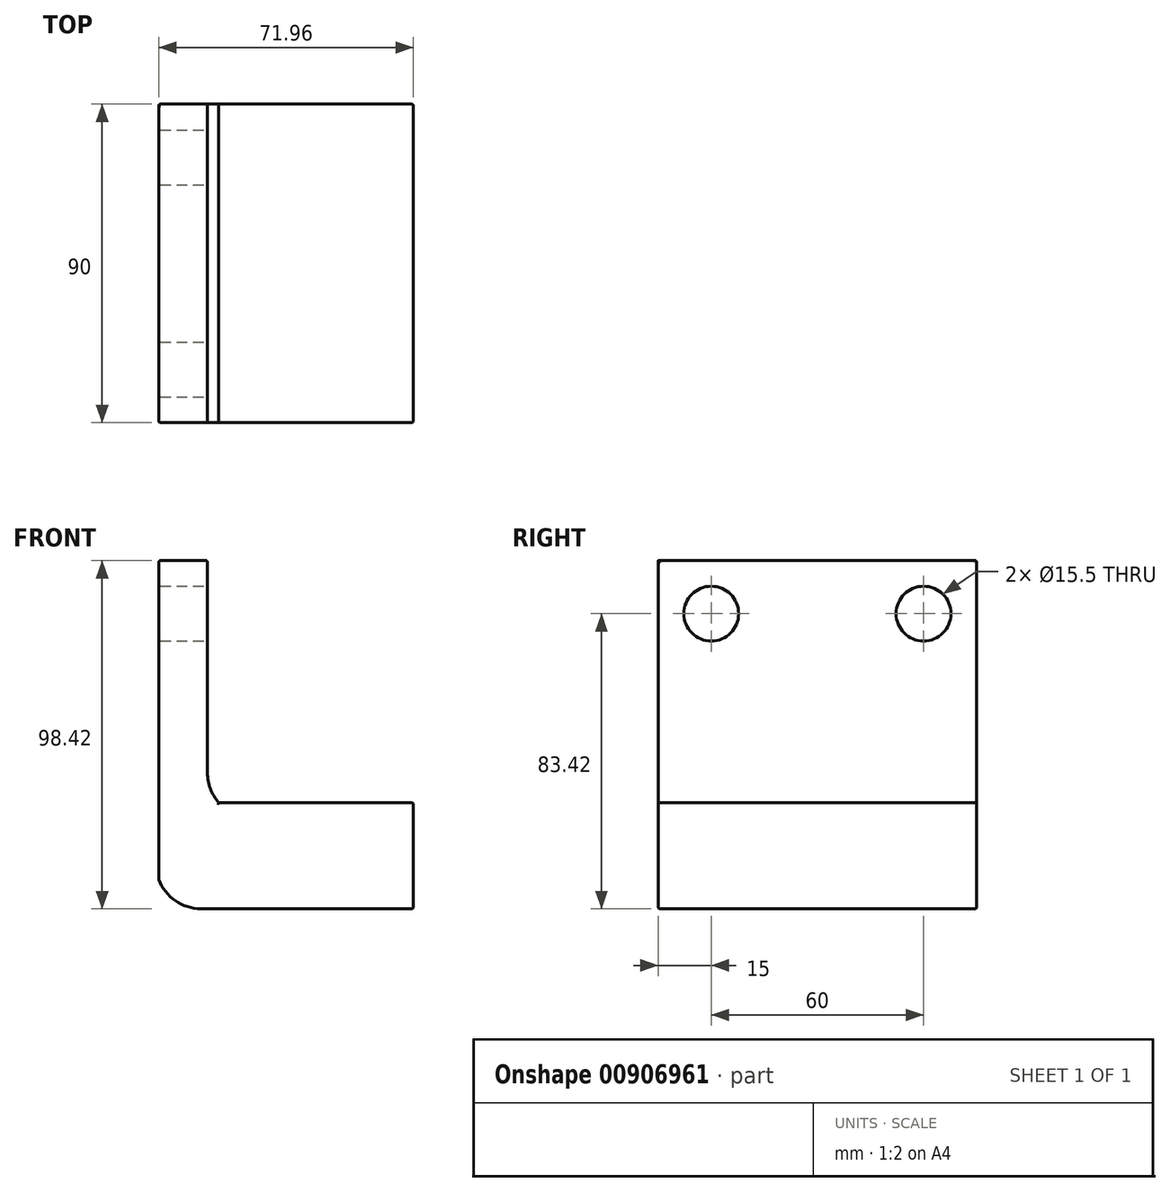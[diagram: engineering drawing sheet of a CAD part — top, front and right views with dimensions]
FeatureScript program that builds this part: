
annotation { "Feature Type Name" : "Feature", "Feature Type Description" : "" }
export const myFeature = defineFeature(function(context is Context, id is Id, definition is map)
    precondition{}
    {
        {
            var Q0;
            Q0=qCreatedBy(makeId("Front.planeOp"),FACE);
            var sketch = newSketch(context, id + "F0", { "sketchPlane" : qUnion([Q0])});
            skLineSegment(sketch, "E0", {"start": v(-41.34, 51.99) * mm, "end": v(-41.34, -21.08) * mm});
            skLineSegment(sketch, "E1", {"start": v(-41.34, 51.99) * mm, "end": v(-27.58, 51.99) * mm});
            skLineSegment(sketch, "E2", {"start": v(-27.58, 51.99) * mm, "end": v(-27.58, -8.01) * mm});
            skLineSegment(sketch, "E3", {"start": v(-24.38, -16.43) * mm, "end": v(30.62, -16.43) * mm});
            skLineSegment(sketch, "E4", {"start": v(30.62, -16.43) * mm, "end": v(30.62, -46.43) * mm});
            skLineSegment(sketch, "E5", {"start": v(30.62, -46.43) * mm, "end": v(-29.38, -46.43) * mm});
            skLineSegment(sketch, "E6", {"start": v(-41.34, -21.08) * mm, "end": v(-41.34, -38.01) * mm});
            skArc(sketch, "E7", {"start": v(-27.58, -8.01) * mm, "mid": v(-26.75, -12.51) * mm, "end": v(-24.38, -16.43) * mm});
            skArc(sketch, "E8", {"start": v(-41.34, -38.01) * mm, "mid": v(-36.7, -44.12) * mm, "end": v(-29.38, -46.43) * mm});
            skSolve(sketch);
        }
        {
            var Q0;
            Q0 = qSketchRegion(id + "F0", true);
            extrude(context, id + "F1", {"entities" : qUnion([Q0]), "depth" : 90 * mm, "offsetDistance" : 25 * mm});
        }
        {
            var Q0;
            Q0=makeQuery(id+"F1.opExtrude","SWEPT_FACE",FACE,{"disambiguationData":[OSD([sQuery(id+"F0.wireOp",EDGE,"E2")])]});
            var sketch = newSketch(context, id + "F2", { "sketchPlane" : qUnion([Q0])});
            skCircle(sketch, "E9", {"center": v(-75, 36.99) * mm, "radius": 7.75 * mm});
            skCircle(sketch, "E10", {"center": v(-15, 36.99) * mm, "radius": 7.75 * mm});
            skSolve(sketch);
        }
        {
            var Q0;
            Q0 = qSketchRegion(id + "F2", true);
            extrude(context, id + "F3", {"entities" : qUnion([Q0]), "operationType" : NewBodyOperationType.REMOVE, "oppositeDirection" : true, "depth" : 25 * mm, "offsetDistance" : 25 * mm});
        }
        {
            var Q0;
            Q0=makeQuery(id+"F1.opExtrude","SWEPT_EDGE",EDGE,{"disambiguationData":[OSD([sQuery(id+"F0.wireOp",EDGE,"E1"),sQuery(id+"F0.wireOp",EDGE,"E2")])]});
            var Q1;
            Q1=makeQuery(id+"F1.opExtrude","CAP_EDGE",EDGE,{"disambiguationData":[OSD([sQuery(id+"F0.wireOp",EDGE,"E2")])],"isStart":true});
            var Q2;
            Q2=makeQuery(id+"F1.opExtrude","CAP_EDGE",EDGE,{"disambiguationData":[OSD([sQuery(id+"F0.wireOp",EDGE,"E2")])],"isStart":false});
            var Q3;
            Q3=makeQuery(id+"F1.opExtrude","SWEPT_EDGE",EDGE,{"disambiguationData":[OSD([sQuery(id+"F0.wireOp",EDGE,"E3"),sQuery(id+"F0.wireOp",EDGE,"E4")])]});
            var Q4;
            Q4=makeQuery(id+"F1.opExtrude","CAP_EDGE",EDGE,{"disambiguationData":[OSD([sQuery(id+"F0.wireOp",EDGE,"E4")])],"isStart":false});
            var Q5;
            Q5=makeQuery(id+"F1.opExtrude","SWEPT_EDGE",EDGE,{"disambiguationData":[OSD([sQuery(id+"F0.wireOp",EDGE,"E4"),sQuery(id+"F0.wireOp",EDGE,"E5")])]});
            var Q6;
            Q6=makeQuery(id+"F1.opExtrude","CAP_EDGE",EDGE,{"disambiguationData":[OSD([sQuery(id+"F0.wireOp",EDGE,"E4")])],"isStart":true});
            var Q7;
            Q7=makeQuery(id+"F1.opExtrude","CAP_EDGE",EDGE,{"disambiguationData":[OSD([sQuery(id+"F0.wireOp",EDGE,"E3")])],"isStart":true});
            var Q8;
            Q8=makeQuery(id+"F1.opExtrude","CAP_EDGE",EDGE,{"disambiguationData":[OSD([sQuery(id+"F0.wireOp",EDGE,"E5")])],"isStart":true});
            var Q9;
            Q9=makeQuery(id+"F1.opExtrude","CAP_EDGE",EDGE,{"disambiguationData":[OSD([sQuery(id+"F0.wireOp",EDGE,"E0"),sQuery(id+"F0.wireOp",EDGE,"E6")])],"isStart":true});
            var Q10;
            Q10=makeQuery(id+"F1.opExtrude","CAP_EDGE",EDGE,{"disambiguationData":[OSD([sQuery(id+"F0.wireOp",EDGE,"E1")])],"isStart":true});
            var Q11;
            Q11=makeQuery(id+"F1.opExtrude","SWEPT_EDGE",EDGE,{"disambiguationData":[OSD([sQuery(id+"F0.wireOp",EDGE,"E0"),sQuery(id+"F0.wireOp",EDGE,"E1")])]});
            var Q12;
            Q12=makeQuery(id+"F1.opExtrude","CAP_EDGE",EDGE,{"disambiguationData":[OSD([sQuery(id+"F0.wireOp",EDGE,"E0"),sQuery(id+"F0.wireOp",EDGE,"E6")])],"isStart":false});
            var Q13;
            Q13=makeQuery(id+"F1.opExtrude","SWEPT_EDGE",EDGE,{"disambiguationData":[OSD([sQuery(id+"F0.wireOp",EDGE,"E6"),sQuery(id+"F0.wireOp",EDGE,"E8")])]});
            var Q14;
            Q14=makeQuery(id+"F1.opExtrude","CAP_EDGE",EDGE,{"disambiguationData":[OSD([sQuery(id+"F0.wireOp",EDGE,"E5")])],"isStart":false});
            var Q15;
            Q15=makeQuery(id+"F1.opExtrude","CAP_EDGE",EDGE,{"disambiguationData":[OSD([sQuery(id+"F0.wireOp",EDGE,"E3")])],"isStart":false});
            fillet(context, id + "F4", {"entities" : qUnion([Q0, Q1, Q2, Q3, Q4, Q5, Q6, Q7, Q8, Q9, Q10, Q11, Q12, Q13, Q14, Q15]), "radius" : 0.5 * mm, "tangentPropagation" : true, "allowEdgeOverflow" : false});
        }
        {
            var Q0;
            Q0=makeQuery(id+"F3.boolean.opBoolean","COPY",EDGE,{"derivedFrom":makeQuery(id+"F3.opExtrude","CAP_EDGE",EDGE,{"disambiguationData":[OSD([sQuery(id+"F2.wireOp",EDGE,"E10")])],"isStart":true})});
            var Q1;
            Q1=makeQuery(id+"F3.boolean.opBoolean","COPY",EDGE,{"derivedFrom":makeQuery(id+"F3.opExtrude","CAP_EDGE",EDGE,{"disambiguationData":[OSD([sQuery(id+"F2.wireOp",EDGE,"E9")])],"isStart":true})});
            var Q2;
            Q2=makeQuery(id+"F3.boolean.opBoolean","INTERSECT",EDGE,{"derivedFrom":[makeQuery(id+"F1.opExtrude","SWEPT_FACE",FACE,{"disambiguationData":[OSD([sQuery(id+"F0.wireOp",EDGE,"E0"),sQuery(id+"F0.wireOp",EDGE,"E6")])]}),makeQuery(id+"F3.opExtrude","SWEPT_FACE",FACE,{"disambiguationData":[OSD([sQuery(id+"F2.wireOp",EDGE,"E9")])]})]});
            var Q3;
            Q3=makeQuery(id+"F3.boolean.opBoolean","INTERSECT",EDGE,{"derivedFrom":[makeQuery(id+"F1.opExtrude","SWEPT_FACE",FACE,{"disambiguationData":[OSD([sQuery(id+"F0.wireOp",EDGE,"E0"),sQuery(id+"F0.wireOp",EDGE,"E6")])]}),makeQuery(id+"F3.opExtrude","SWEPT_FACE",FACE,{"disambiguationData":[OSD([sQuery(id+"F2.wireOp",EDGE,"E10")])]})]});
            fillet(context, id + "F5", {"entities" : qUnion([Q0, Q1, Q2, Q3]), "radius" : 0.5 * mm, "tangentPropagation" : true, "allowEdgeOverflow" : false});
        }
    });
